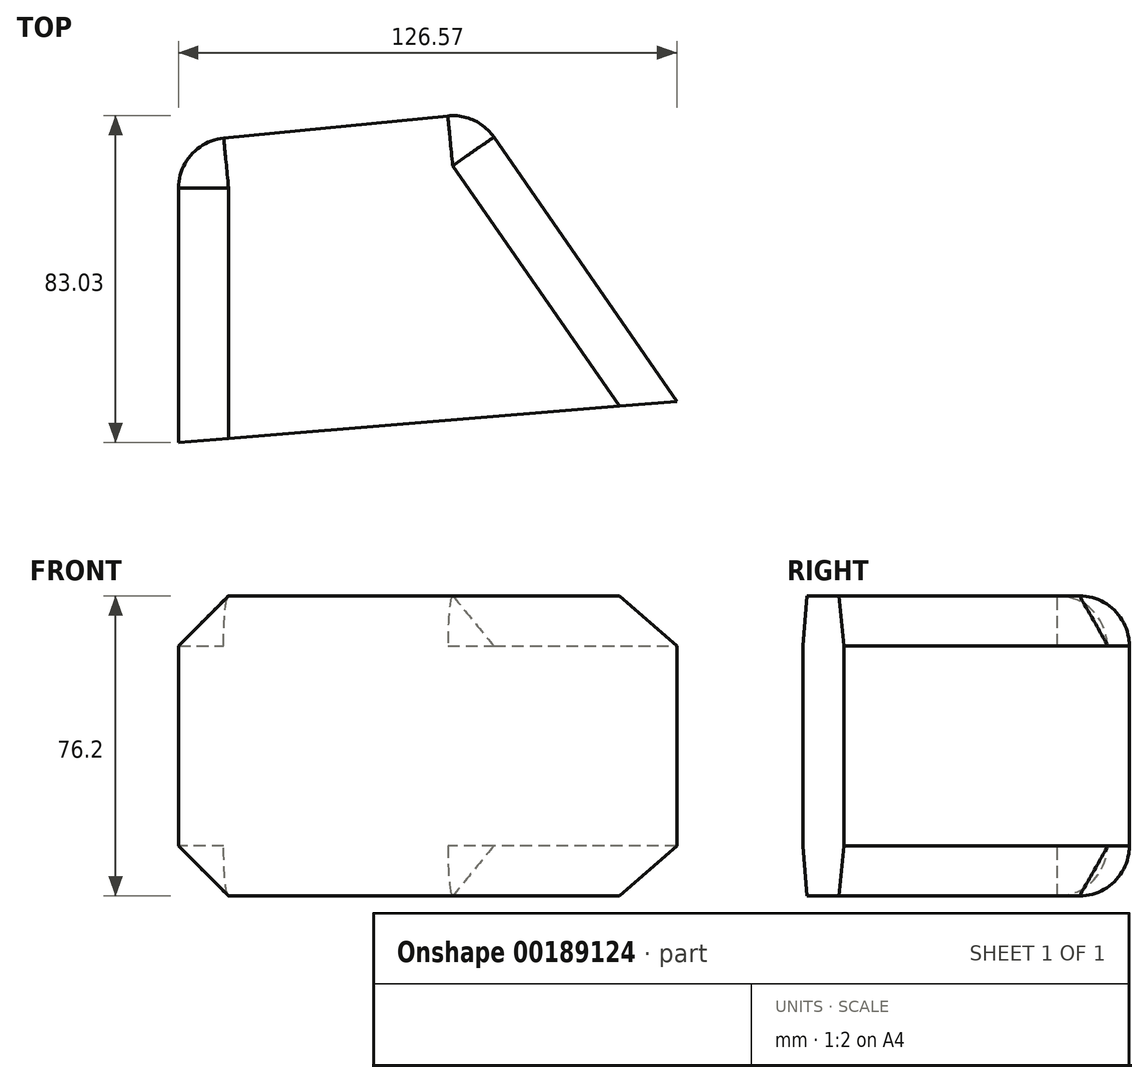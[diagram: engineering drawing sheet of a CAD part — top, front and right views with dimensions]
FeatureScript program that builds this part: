
annotation { "Feature Type Name" : "Feature", "Feature Type Description" : "" }
export const myFeature = defineFeature(function(context is Context, id is Id, definition is map)
    precondition{}
    {
        {
            var Q0;
            Q0=qCreatedBy(makeId("Top.planeOp"),FACE);
            var sketch = newSketch(context, id + "F0", { "sketchPlane" : qUnion([Q0])});
            skLineSegment(sketch, "E0", {"start": v(0, 0) * mm, "end": v(-126.57, -10.4) * mm});
            skLineSegment(sketch, "E1", {"start": v(-126.57, -10.4) * mm, "end": v(-126.57, 65.8) * mm});
            skLineSegment(sketch, "E2", {"start": v(-126.57, 65.8) * mm, "end": v(-50.74, 73.3) * mm});
            skLineSegment(sketch, "E3", {"start": v(-50.74, 73.3) * mm, "end": v(0, 0) * mm});
            skSolve(sketch);
        }
        {
            var Q0;
            Q0 = qSketchRegion(id + "F0", true);
            extrude(context, id + "F1", {"entities" : qUnion([Q0]), "endBound" : BoundingType.SYMMETRIC, "depth" : 76.2 * mm});
        }
        {
            var Q0;
            Q0=makeQuery(id+"F1.split0.splitOp","SPLIT",EDGE,{"derivedFrom":makeQuery(id+"F1.opExtrude","SWEPT_EDGE",EDGE,{"disambiguationData":[OSD([sQuery(id+"F0.wireOp",EDGE,"E2"),sQuery(id+"F0.wireOp",EDGE,"E3")])]})});
            var Q1;
            Q1=makeQuery(id+"F1.split0.splitOp","SPLIT",EDGE,{"derivedFrom":makeQuery(id+"F1.opExtrude","SWEPT_EDGE",EDGE,{"disambiguationData":[OSD([sQuery(id+"F0.wireOp",EDGE,"E2"),sQuery(id+"F0.wireOp",EDGE,"E3")])]}),"isFromBackBody":true});
            var Q2;
            Q2=makeQuery(id+"F1.opExtrude","CAP_EDGE",EDGE,{"disambiguationData":[OSD([sQuery(id+"F0.wireOp",EDGE,"E2")])],"isStart":true});
            var Q3;
            Q3=makeQuery(id+"F1.opExtrude","CAP_EDGE",EDGE,{"disambiguationData":[OSD([sQuery(id+"F0.wireOp",EDGE,"E2")])],"isStart":false});
            var Q4;
            Q4=makeQuery(id+"F1.split0.splitOp","SPLIT",EDGE,{"derivedFrom":makeQuery(id+"F1.opExtrude","SWEPT_EDGE",EDGE,{"disambiguationData":[OSD([sQuery(id+"F0.wireOp",EDGE,"E1"),sQuery(id+"F0.wireOp",EDGE,"E2")])]})});
            var Q5;
            Q5=makeQuery(id+"F1.split0.splitOp","SPLIT",EDGE,{"derivedFrom":makeQuery(id+"F1.opExtrude","SWEPT_EDGE",EDGE,{"disambiguationData":[OSD([sQuery(id+"F0.wireOp",EDGE,"E1"),sQuery(id+"F0.wireOp",EDGE,"E2")])]}),"isFromBackBody":true});
            fillet(context, id + "F2", {"entities" : qUnion([Q0, Q1, Q2, Q3, Q4, Q5]), "radius" : 12.7 * mm, "tangentPropagation" : true, "allowEdgeOverflow" : false});
        }
        {
            var Q0;
            Q0=makeQuery(id+"F1.opExtrude","CAP_EDGE",EDGE,{"disambiguationData":[OSD([sQuery(id+"F0.wireOp",EDGE,"E1")])],"isStart":false});
            var Q1;
            Q1=makeQuery(id+"F1.opExtrude","CAP_EDGE",EDGE,{"disambiguationData":[OSD([sQuery(id+"F0.wireOp",EDGE,"E1")])],"isStart":true});
            var Q2;
            Q2=makeQuery(id+"F1.opExtrude","CAP_EDGE",EDGE,{"disambiguationData":[OSD([sQuery(id+"F0.wireOp",EDGE,"E3")])],"isStart":false});
            var Q3;
            Q3=makeQuery(id+"F1.opExtrude","CAP_EDGE",EDGE,{"disambiguationData":[OSD([sQuery(id+"F0.wireOp",EDGE,"E3")])],"isStart":true});
            chamfer(context, id + "F3", {"entities" : qUnion([Q0, Q1, Q2, Q3]), "width" : 12.7 * mm, "tangentPropagation" : true});
        }
    });
